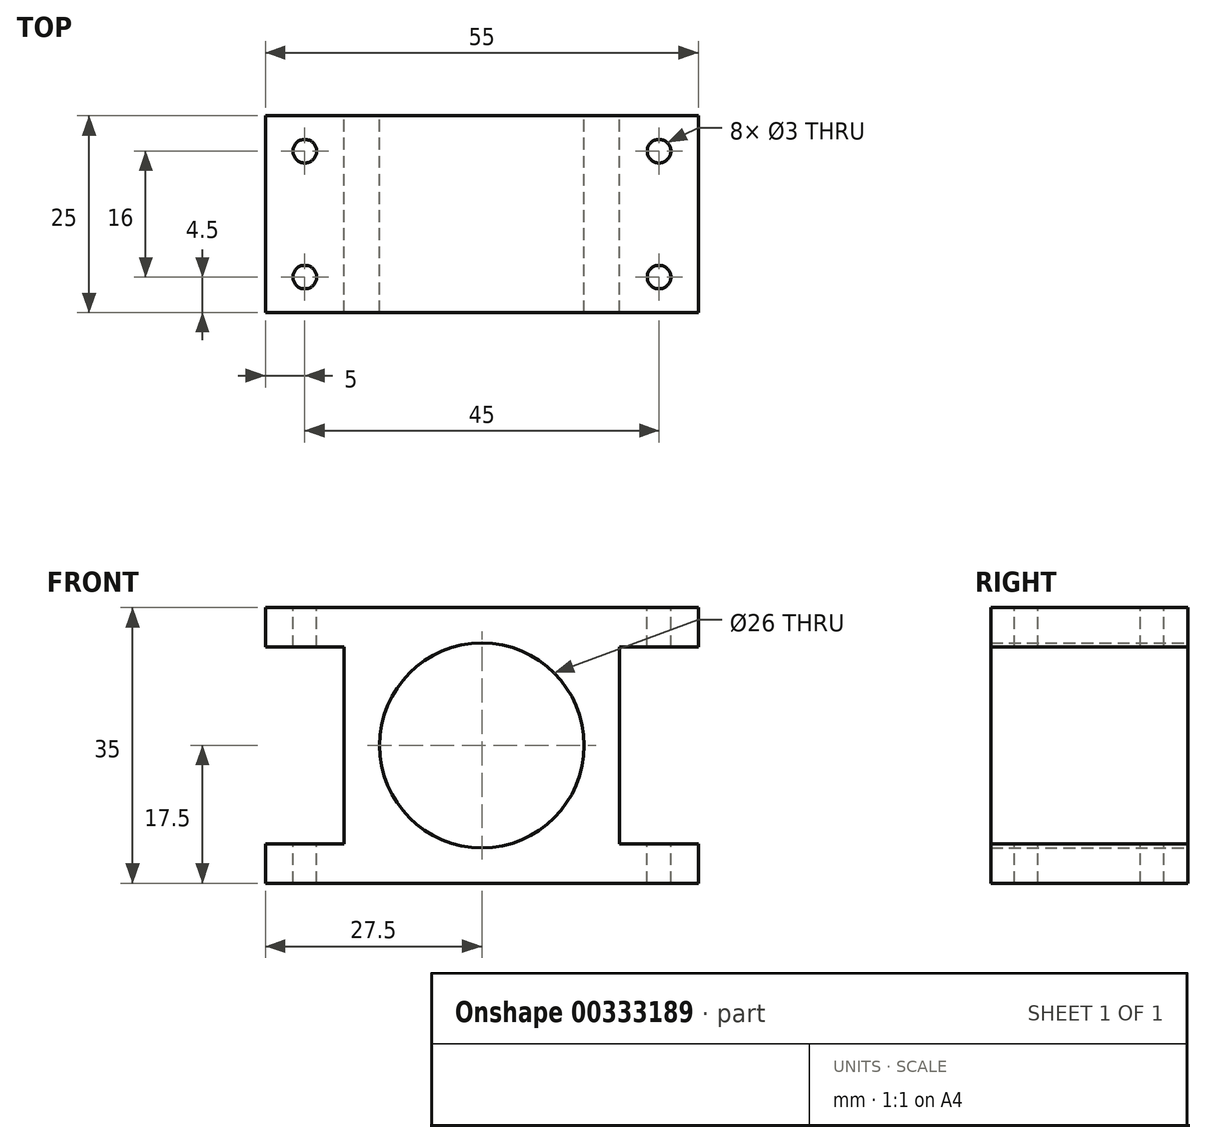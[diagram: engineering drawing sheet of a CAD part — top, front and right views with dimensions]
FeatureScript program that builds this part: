
annotation { "Feature Type Name" : "Feature", "Feature Type Description" : "" }
export const myFeature = defineFeature(function(context is Context, id is Id, definition is map)
    precondition{}
    {
        {
            var Q0;
            Q0=qCreatedBy(makeId("Front.planeOp"),FACE);
            var sketch = newSketch(context, id + "F0", { "sketchPlane" : qUnion([Q0])});
            skCircle(sketch, "E0", {"center": v(0, 0) * mm, "radius": 13 * mm});
            skLineSegment(sketch, "E1.bottom", {"start": v(17.5, -17.5) * mm, "end": v(-17.5, -17.5) * mm});
            skLineSegment(sketch, "E1.top", {"start": v(17.5, 17.5) * mm, "end": v(-17.5, 17.5) * mm});
            skLineSegment(sketch, "E1.left", {"start": v(17.5, -17.5) * mm, "end": v(17.5, 17.5) * mm});
            skLineSegment(sketch, "E1.right", {"start": v(-17.5, -17.5) * mm, "end": v(-17.5, 17.5) * mm});
            skLineSegment(sketch, "E2", {"start": v(-17.5, 17.5) * mm, "end": v(-27.5, 17.5) * mm});
            skLineSegment(sketch, "E3", {"start": v(-27.5, 17.5) * mm, "end": v(-27.5, 12.5) * mm});
            skLineSegment(sketch, "E4", {"start": v(-27.5, -17.5) * mm, "end": v(-17.5, -17.5) * mm});
            skLineSegment(sketch, "E5", {"start": v(-27.5, 12.5) * mm, "end": v(-17.5, 12.5) * mm});
            skLineSegment(sketch, "E6.MirrorCS", {"start": v(-27.5, -12.5) * mm, "end": v(-17.5, -12.5) * mm});
            skLineSegment(sketch, "E7.MirrorCS", {"start": v(27.5, 12.5) * mm, "end": v(17.5, 12.5) * mm});
            skLineSegment(sketch, "E8.MirrorCS", {"start": v(27.5, 17.5) * mm, "end": v(27.5, 12.5) * mm});
            skLineSegment(sketch, "E9.MirrorCS", {"start": v(17.5, 17.5) * mm, "end": v(27.5, 17.5) * mm});
            skLineSegment(sketch, "E10.MirrorCS", {"start": v(27.5, -12.5) * mm, "end": v(17.5, -12.5) * mm});
            skLineSegment(sketch, "E11.MirrorCS", {"start": v(27.5, -17.5) * mm, "end": v(17.5, -17.5) * mm});
            skLineSegment(sketch, "E12.trimOffspring", {"start": v(-27.5, -12.5) * mm, "end": v(-27.5, -17.5) * mm});
            skLineSegment(sketch, "E13.trimOffspring", {"start": v(27.5, -12.5) * mm, "end": v(27.5, -17.5) * mm});
            skSolve(sketch);
        }
        {
            var Q0;
            Q0=qSketchRegion(id+"F0",true);
            extrude(context, id + "F1", {"entities" : qUnion([Q0]), "endBound" : BoundingType.SYMMETRIC, "depth" : 25 * mm});
        }
        {
            var Q0;
            Q0=makeQuery(id+"F1.opExtrude","SWEPT_FACE",FACE,{"disambiguationData":[OSD([sQuery(id+"F0.wireOp",EDGE,"E1.top"),sQuery(id+"F0.wireOp",EDGE,"E2"),sQuery(id+"F0.wireOp",EDGE,"E9.MirrorCS")])]});
            var sketch = newSketch(context, id + "F2", { "sketchPlane" : qUnion([Q0])});
            skCircle(sketch, "E14", {"center": v(-22.5, -8) * mm, "radius": 1.5 * mm});
            skCircle(sketch, "E15.MirrorC", {"center": v(-22.5, 8) * mm, "radius": 1.5 * mm});
            skCircle(sketch, "E16.MirrorC", {"center": v(22.5, 8) * mm, "radius": 1.5 * mm});
            skCircle(sketch, "E17.MirrorC", {"center": v(22.5, -8) * mm, "radius": 1.5 * mm});
            skSolve(sketch);
        }
        {
            var Q0;
            Q0=qSketchRegion(id+"F2",true);
            extrude(context, id + "F3", {"entities" : qUnion([Q0]), "operationType" : NewBodyOperationType.REMOVE, "oppositeDirection" : true, "depth" : 45.1 * mm});
        }
    });
